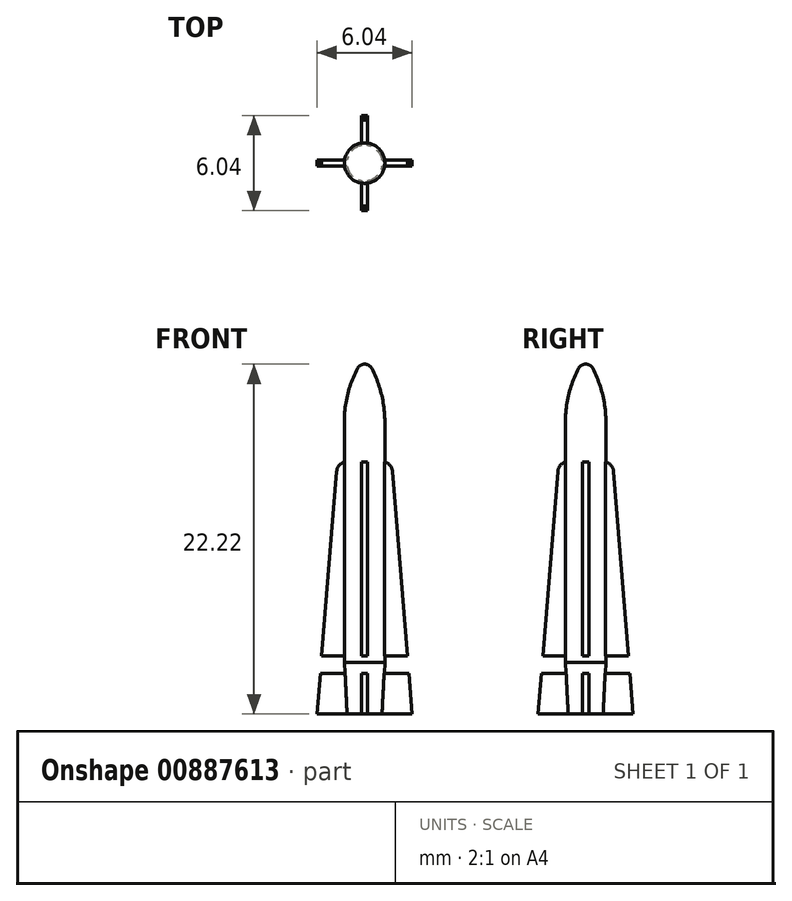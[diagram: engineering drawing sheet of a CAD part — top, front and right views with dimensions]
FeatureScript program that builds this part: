
annotation { "Feature Type Name" : "Feature", "Feature Type Description" : "" }
export const myFeature = defineFeature(function(context is Context, id is Id, definition is map)
    precondition{}
    {
        {
            var Q0;
            Q0=qCreatedBy(makeId("Front.planeOp"),FACE);
            var sketch = newSketch(context, id + "F0", { "sketchPlane" : qUnion([Q0])});
            skLineSegment(sketch, "E0", {"start": v(0, 0) * mm, "end": v(0, 22.22) * mm});
            skLineSegment(sketch, "E1", {"start": v(1.28, 18.54) * mm, "end": v(1.28, 0) * mm});
            skLineSegment(sketch, "E2", {"start": v(1.28, 0) * mm, "end": v(0, 0) * mm});
            skLineSegment(sketch, "E3", {"start": v(1.28, 3.26) * mm, "end": v(1.13, 0) * mm});
            skArc(sketch, "E4", {"start": v(0.46, 21.94) * mm, "mid": v(0.27, 22.15) * mm, "end": v(0, 22.22) * mm});
            skArc(sketch, "E5", {"start": v(1.28, 18.54) * mm, "mid": v(1.07, 20.3) * mm, "end": v(0.46, 21.94) * mm});
            skSolve(sketch);
        }
        {
            var Q0;
            {var subQ0=sQuery(id+"F0.wireOp",EDGE,"mrwio9nY-PsAZ-Zbfy-NhIU-sYq0QVbgGXAG");Q0=makeQuery(id+"F0.imprint","IMPRINT",FACE,{"disambiguationData":[TD([[makeQuery(id+"F0.imprint","IMPRINT",EDGE,{"derivedFrom":subQ0}),-1.0]])]});}
            var Q1;
            {var subQ7=sQuery(id+"F0.wireOp",EDGE,"E0");Q1=makeQuery(id+"F0.imprint","IMPRINT",FACE,{"disambiguationData":[TD([[makeQuery(id+"F0.imprint","IMPRINT",EDGE,{"derivedFrom":subQ7}),-1.0]])]});}
            var Q2;
            Q2=sQuery(id+"F0.wireOp",EDGE,"E0");
            revolve(context, id + "F1", {"surfaceOperationType" : NewSurfaceOperationType.NEW, "entities" : qUnion([Q0, Q1]), "axis" : qUnion([Q2]), "revolveType" : RevolveType.FULL});
        }
        {
            var Q0;
            Q0=qCreatedBy(makeId("Front.planeOp"),FACE);
            var sketch = newSketch(context, id + "F2", { "sketchPlane" : qUnion([Q0])});
            skLineSegment(sketch, "E6", {"start": v(0, 0) * mm, "end": v(0, 16.03) * mm});
            skLineSegment(sketch, "E7", {"start": v(0.4, 3.68) * mm, "end": v(0.4, 2.57) * mm});
            skLineSegment(sketch, "E8", {"start": v(0.4, 2.57) * mm, "end": v(2.81, 2.57) * mm});
            skLineSegment(sketch, "E9", {"start": v(1.28, 0) * mm, "end": v(1.28, 32.87) * mm, "construction": true});
            skLineSegment(sketch, "E10", {"start": v(0.4, 3.68) * mm, "end": v(2.72, 3.68) * mm});
            skLineSegment(sketch, "E11", {"start": v(2.72, 3.68) * mm, "end": v(1.77, 15.42) * mm});
            skLineSegment(sketch, "E12", {"start": v(0, 0) * mm, "end": v(3.02, 0) * mm});
            skLineSegment(sketch, "E13.0", {"start": v(1.28, 3.26) * mm, "end": v(-1.28, 3.26) * mm});
            skLineSegment(sketch, "E14.0", {"start": v(0.46, 21.94) * mm, "end": v(-0.46, 21.94) * mm});
            skLineSegment(sketch, "E15", {"start": v(0, 16.03) * mm, "end": v(1.11, 16.03) * mm});
            skArc(sketch, "E16", {"start": v(1.77, 15.42) * mm, "mid": v(1.56, 15.85) * mm, "end": v(1.11, 16.03) * mm});
            skLineSegment(sketch, "E17", {"start": v(2.81, 2.57) * mm, "end": v(3.02, 0) * mm});
            skSolve(sketch);
        }
        {
            var Q0;
            Q0=qSketchRegion(id+"F2",true);
            extrude(context, id + "F3", {"entities" : qUnion([Q0]), "operationType" : NewBodyOperationType.ADD, "depth" : .4 * mm, "offsetDistance" : 25 * mm, "symmetric" : true});
        }
        {
            var Q0;
            Q0=makeQuery(id+"F1.opRevolve","SWEPT_BODY",BODY,{"disambiguationData":[OSD([sQuery(id+"F0.wireOp",EDGE,"E0"),sQuery(id+"F0.wireOp",EDGE,"E1"),sQuery(id+"F0.wireOp",EDGE,"E2"),sQuery(id+"F0.wireOp",EDGE,"2EiOItwe-9FNA-eY8p-DkXH-AMy5AHyUmzZA"),sQuery(id+"F0.wireOp",EDGE,"lF35QjYl-MEgV-fRWE-0Yr6-Bt5vS8A7brRf")])]});
            var Q1;
            Q1=makeQuery(id+"F1.opRevolve","SWEPT_FACE",FACE,{"disambiguationData":[OSD([sQuery(id+"F0.wireOp",EDGE,"E1")])]});
            circularPattern(context, id + "F4", {"operationType" : NewBodyOperationType.ADD, "entities" : qUnion([Q0]), "axis" : qUnion([Q1]), "angle" : 360 * degree, "instanceCount" : 4, "equalSpace" : true, "computeTransformsWithoutBuiltin" : true});
        }
    });
